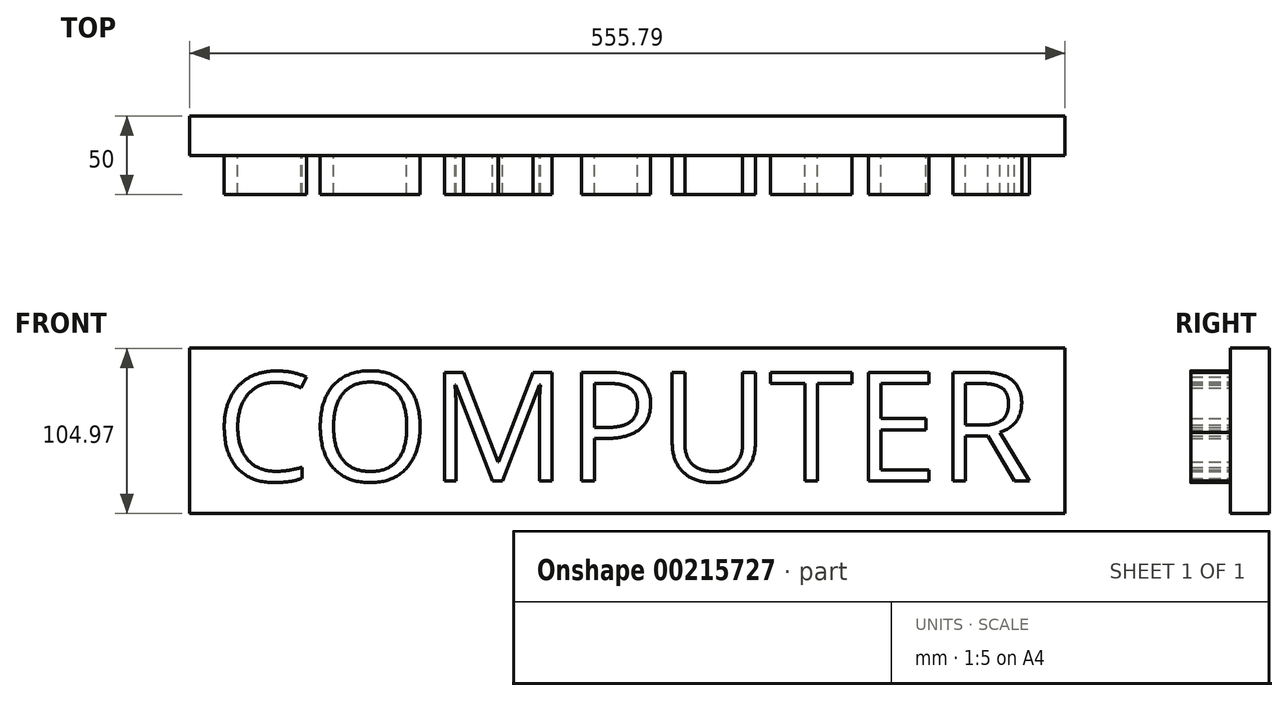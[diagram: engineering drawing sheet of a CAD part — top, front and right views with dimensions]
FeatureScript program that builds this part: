
annotation { "Feature Type Name" : "Feature", "Feature Type Description" : "" }
export const myFeature = defineFeature(function(context is Context, id is Id, definition is map)
    precondition{}
    {
        {
            var Q0;
            Q0=qCreatedBy(makeId("Front.planeOp"),FACE);
            var sketch = newSketch(context, id + "F0", { "sketchPlane" : qUnion([Q0])});
            skLineSegment(sketch, "E0.bottom", {"start": v(0, 0) * mm, "end": v(555.79, 0) * mm});
            skLineSegment(sketch, "E0.top", {"start": v(0, 104.97) * mm, "end": v(555.79, 104.97) * mm});
            skLineSegment(sketch, "E0.left", {"start": v(0, 0) * mm, "end": v(0, 104.97) * mm});
            skLineSegment(sketch, "E0.right", {"start": v(555.79, 0) * mm, "end": v(555.79, 104.97) * mm});
            skSolve(sketch);
        }
        {
            var Q0;
            Q0=qCreatedBy(makeId("Front.planeOp"),FACE);
            var sketch = newSketch(context, id + "F1", { "sketchPlane" : qUnion([Q0])});
            skText(sketch, "E1", { "text": "COMPUTER", "fontName": "OpenSans-Regular.ttf"});
            const initialGuessF1  = {"E1": [0.01597, 0.02059, 1, 0, 0.06957]};
            skSetInitialGuess(sketch, initialGuessF1);
            skSolve(sketch);
        }
        {
            var Q0;
            Q0 = qSketchRegion(id + "F0", true);
            extrude(context, id + "F2", {"entities" : qUnion([Q0]), "oppositeDirection" : true, "depth" : 25 * mm});
        }
        {
            var Q0;
            Q0 = qSketchRegion(id + "F1", true);
            extrude(context, id + "F3", {"entities" : qUnion([Q0]), "operationType" : NewBodyOperationType.ADD, "depth" : 25 * mm});
        }
    });
